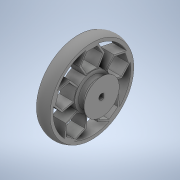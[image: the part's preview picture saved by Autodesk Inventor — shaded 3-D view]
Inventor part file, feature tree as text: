
AUTODESK INVENTOR PART (.ipt)
format: ipt  version: 2020 (Build 240168000, 168)  size: 439,296 bytes
history: native  units: in
note: dims shown in document units (in); Inventor stores cm internally (conversion verified against a paired STEP export)
features: sketch x4, extrude x2, revolve x2, projected_geometry x1
ambient origin geometry x8: Origin, YZ Plane, XZ Plane, XY Plane, X Axis, Y Axis, Z Axis, Center Point
bodies: Solid1 (feature_tree)
feature tree (9):
  extrude  "Extrusion1"  Depth=0.0394in
  sketch  "Sketch3"  dims[d6=0.7087in d7=0.1969in]
  revolve  "Revolution1"  [1 undecoded]
  extrude  "Extrusion2"  Depth=0.1969in
  revolve  "Revolution2"  [1 undecoded]
  sketch  "Sketch1"  dims[d0=0.1181in d1=0.0394in]
  sketch  "Sketch2"  dims[d3=1.6929in d4=0.1181in]
  projected_geometry  "Projected Loop1"
  sketch  "Sketch4"  dims[d8=0.0in d9=1.6929in d10=0.063in d11=0.0315in d16=0.2756in d17=0.0in d19=360.0deg d20=0.0984in d24=0.0394in d25=90.0deg d26=45.0deg d28=0.0079in d29=1.9685in d31=360.0deg]
note: 2 required parameter values undecoded (feature->parameter linkage not recoverable at this tier; creation-order binding heuristic only, values carry confidence <= 0.55)
